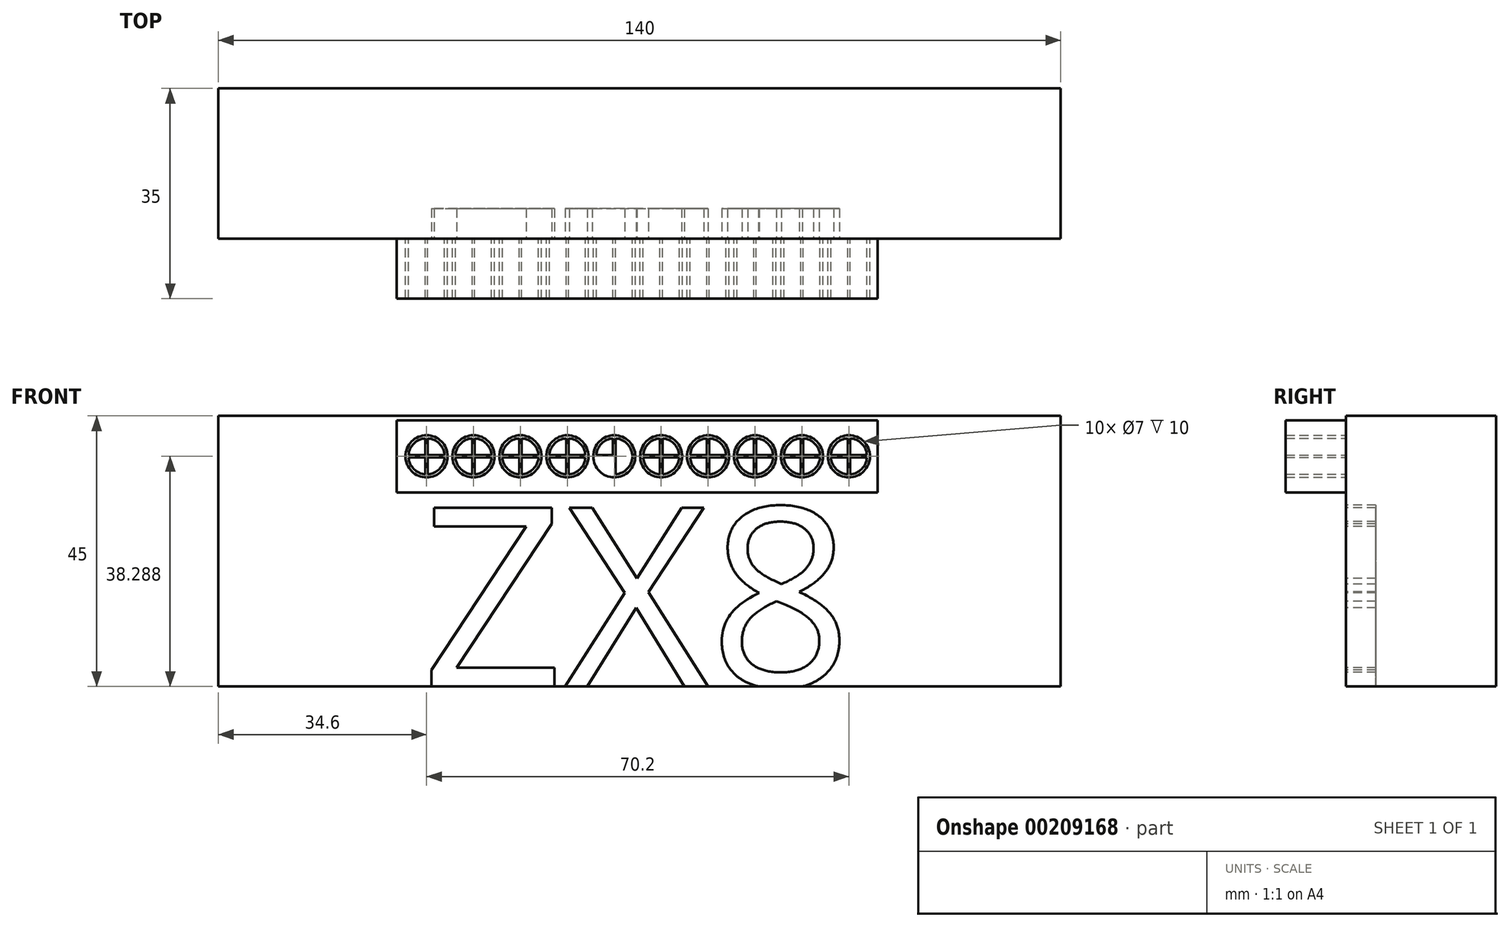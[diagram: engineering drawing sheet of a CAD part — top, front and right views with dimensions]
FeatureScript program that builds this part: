
annotation { "Feature Type Name" : "Feature", "Feature Type Description" : "" }
export const myFeature = defineFeature(function(context is Context, id is Id, definition is map)
    precondition{}
    {
        {
            var Q0;
            Q0=qCreatedBy(makeId("Front.planeOp"),FACE);
            var sketch = newSketch(context, id + "F0", { "sketchPlane" : qUnion([Q0])});
            skLineSegment(sketch, "E0.bottom", {"start": v(70, 22.5) * mm, "end": v(-70, 22.5) * mm});
            skLineSegment(sketch, "E0.top", {"start": v(70, -22.5) * mm, "end": v(-70, -22.5) * mm});
            skLineSegment(sketch, "E0.left", {"start": v(70, 22.5) * mm, "end": v(70, -22.5) * mm});
            skLineSegment(sketch, "E0.right", {"start": v(-70, 22.5) * mm, "end": v(-70, -22.5) * mm});
            skPoint(sketch, "E0.middle", {"position": v(0, 0) * mm});
            skSolve(sketch);
        }
        {
            var Q0;
            Q0 = qSketchRegion(id + "F0", true);
            extrude(context, id + "F1", {"entities" : qUnion([Q0]), "depth" : 25 * mm});
        }
        {
            var Q0;
            Q0=makeQuery(id+"F1.opExtrude","CAP_FACE",FACE,{"disambiguationData":[OSD([sQuery(id+"F0.wireOp",EDGE,"E0.bottom"),sQuery(id+"F0.wireOp",EDGE,"E0.top"),sQuery(id+"F0.wireOp",EDGE,"E0.left"),sQuery(id+"F0.wireOp",EDGE,"E0.right")])],"isStart":false});
            var sketch = newSketch(context, id + "F2", { "sketchPlane" : qUnion([Q0])});
            skText(sketch, "E1", { "text": "ZX8", "fontName": "OpenSans-Regular.ttf"});
            const initialGuessF2  = {"E1": [-0.03628, -0.0225, 1, 0, 0.03]};
            skSetInitialGuess(sketch, initialGuessF2);
            skSolve(sketch);
        }
        {
            var Q0;
            Q0 = qSketchRegion(id + "F2", true);
            extrude(context, id + "F3", {"entities" : qUnion([Q0]), "operationType" : NewBodyOperationType.REMOVE, "oppositeDirection" : true, "depth" : 5 * mm});
        }
        {
            var Q0;
            {var subQ0=sQuery(id+"F0.wireOp",EDGE,"E0.left");var subQ1=sQuery(id+"F0.wireOp",EDGE,"E0.bottom");var subQ2=sQuery(id+"F0.wireOp",EDGE,"E0.right");var subQ3=sQuery(id+"F0.wireOp",EDGE,"E0.top");Q0=makeQuery(id+"F3.boolean.opBoolean","SPLIT",FACE,{"disambiguationData":[TD([makeQuery(id+"F1.opExtrude","SWEPT_FACE",FACE,{"disambiguationData":[OSD([subQ1])]})])],"derivedFrom":makeQuery(id+"F1.opExtrude","CAP_FACE",FACE,{"disambiguationData":[OSD([subQ1,subQ3,subQ0,subQ2])],"isStart":false})});}
            var sketch = newSketch(context, id + "F4", { "sketchPlane" : qUnion([Q0])});
            skLineSegment(sketch, "E2.bottom", {"start": v(-40.4, 21.79) * mm, "end": v(39.6, 21.79) * mm});
            skLineSegment(sketch, "E2.top", {"start": v(-40.4, 9.79) * mm, "end": v(39.6, 9.79) * mm});
            skLineSegment(sketch, "E2.left", {"start": v(-40.4, 21.79) * mm, "end": v(-40.4, 9.79) * mm});
            skLineSegment(sketch, "E2.right", {"start": v(39.6, 21.79) * mm, "end": v(39.6, 9.79) * mm});
            skCircle(sketch, "E3", {"center": v(-35.4, 15.79) * mm, "radius": 3 * mm});
            skLineSegment(sketch, "E4.0", {"start": v(-35.6, 18.79) * mm, "end": v(-35.6, 12.79) * mm});
            skLineSegment(sketch, "E5.0", {"start": v(-35.2, 18.79) * mm, "end": v(-35.2, 12.79) * mm});
            skLineSegment(sketch, "E6.0", {"start": v(-38.4, 15.59) * mm, "end": v(-32.4, 15.59) * mm});
            skLineSegment(sketch, "E7.0", {"start": v(-38.4, 15.99) * mm, "end": v(-32.4, 15.99) * mm});
            skCircle(sketch, "E8.1.0.0", {"center": v(-27.6, 15.79) * mm, "radius": 3 * mm});
            skLineSegment(sketch, "E8.1.0.1", {"start": v(-30.6, 15.99) * mm, "end": v(-24.6, 15.99) * mm});
            skLineSegment(sketch, "E8.1.0.2", {"start": v(-27.4, 18.79) * mm, "end": v(-27.4, 12.79) * mm});
            skLineSegment(sketch, "E8.1.0.3", {"start": v(-27.8, 18.79) * mm, "end": v(-27.8, 12.79) * mm});
            skLineSegment(sketch, "E8.1.0.4", {"start": v(-30.6, 15.59) * mm, "end": v(-24.6, 15.59) * mm});
            skCircle(sketch, "E8.2.0.0", {"center": v(-19.8, 15.79) * mm, "radius": 3 * mm});
            skLineSegment(sketch, "E8.2.0.1", {"start": v(-22.8, 15.99) * mm, "end": v(-16.8, 15.99) * mm});
            skLineSegment(sketch, "E8.2.0.2", {"start": v(-19.6, 18.79) * mm, "end": v(-19.6, 12.79) * mm});
            skLineSegment(sketch, "E8.2.0.3", {"start": v(-20, 18.79) * mm, "end": v(-20, 12.79) * mm});
            skLineSegment(sketch, "E8.2.0.4", {"start": v(-22.8, 15.59) * mm, "end": v(-16.8, 15.59) * mm});
            skCircle(sketch, "E8.3.0.0", {"center": v(-12, 15.79) * mm, "radius": 3 * mm});
            skLineSegment(sketch, "E8.3.0.1", {"start": v(-15, 15.99) * mm, "end": v(-9, 15.99) * mm});
            skLineSegment(sketch, "E8.3.0.2", {"start": v(-11.8, 18.79) * mm, "end": v(-11.8, 12.79) * mm});
            skLineSegment(sketch, "E8.3.0.3", {"start": v(-12.2, 18.79) * mm, "end": v(-12.2, 12.79) * mm});
            skLineSegment(sketch, "E8.3.0.4", {"start": v(-15, 15.59) * mm, "end": v(-9, 15.59) * mm});
            skCircle(sketch, "E8.4.0.0", {"center": v(-4.2, 15.79) * mm, "radius": 3 * mm});
            skLineSegment(sketch, "E8.4.0.1", {"start": v(-7.2, 15.99) * mm, "end": v(-1.2, 15.99) * mm});
            skLineSegment(sketch, "E8.4.0.2", {"start": v(-4, 18.79) * mm, "end": v(-4, 12.79) * mm});
            skLineSegment(sketch, "E8.4.0.3", {"start": v(-4.4, 18.79) * mm, "end": v(-4.4, 12.79) * mm});
            skLineSegment(sketch, "E8.4.0.4", {"start": v(-7.2, 15.59) * mm, "end": v(-1.2, 15.59) * mm});
            skCircle(sketch, "E8.5.0.0", {"center": v(3.6, 15.79) * mm, "radius": 3 * mm});
            skLineSegment(sketch, "E8.5.0.1", {"start": v(0.6, 15.99) * mm, "end": v(6.6, 15.99) * mm});
            skLineSegment(sketch, "E8.5.0.2", {"start": v(3.8, 18.79) * mm, "end": v(3.8, 12.79) * mm});
            skLineSegment(sketch, "E8.5.0.3", {"start": v(3.4, 18.79) * mm, "end": v(3.4, 12.79) * mm});
            skLineSegment(sketch, "E8.5.0.4", {"start": v(0.6, 15.59) * mm, "end": v(6.6, 15.59) * mm});
            skCircle(sketch, "E8.6.0.0", {"center": v(11.4, 15.79) * mm, "radius": 3 * mm});
            skLineSegment(sketch, "E8.6.0.1", {"start": v(8.4, 15.99) * mm, "end": v(14.4, 15.99) * mm});
            skLineSegment(sketch, "E8.6.0.2", {"start": v(11.6, 18.79) * mm, "end": v(11.6, 12.79) * mm});
            skLineSegment(sketch, "E8.6.0.3", {"start": v(11.2, 18.79) * mm, "end": v(11.2, 12.79) * mm});
            skLineSegment(sketch, "E8.6.0.4", {"start": v(8.4, 15.59) * mm, "end": v(14.4, 15.59) * mm});
            skCircle(sketch, "E8.7.0.0", {"center": v(19.2, 15.79) * mm, "radius": 3 * mm});
            skLineSegment(sketch, "E8.7.0.1", {"start": v(16.2, 15.99) * mm, "end": v(22.2, 15.99) * mm});
            skLineSegment(sketch, "E8.7.0.2", {"start": v(19.4, 18.79) * mm, "end": v(19.4, 12.79) * mm});
            skLineSegment(sketch, "E8.7.0.3", {"start": v(19, 18.79) * mm, "end": v(19, 12.79) * mm});
            skLineSegment(sketch, "E8.7.0.4", {"start": v(16.2, 15.59) * mm, "end": v(22.2, 15.59) * mm});
            skCircle(sketch, "E8.8.0.0", {"center": v(27, 15.79) * mm, "radius": 3 * mm});
            skLineSegment(sketch, "E8.8.0.1", {"start": v(24, 15.99) * mm, "end": v(30, 15.99) * mm});
            skLineSegment(sketch, "E8.8.0.2", {"start": v(27.2, 18.79) * mm, "end": v(27.2, 12.79) * mm});
            skLineSegment(sketch, "E8.8.0.3", {"start": v(26.8, 18.79) * mm, "end": v(26.8, 12.79) * mm});
            skLineSegment(sketch, "E8.8.0.4", {"start": v(24, 15.59) * mm, "end": v(30, 15.59) * mm});
            skCircle(sketch, "E8.9.0.0", {"center": v(34.8, 15.79) * mm, "radius": 3 * mm});
            skLineSegment(sketch, "E8.9.0.1", {"start": v(31.8, 15.99) * mm, "end": v(37.8, 15.99) * mm});
            skLineSegment(sketch, "E8.9.0.2", {"start": v(35, 18.79) * mm, "end": v(35, 12.79) * mm});
            skLineSegment(sketch, "E8.9.0.3", {"start": v(34.6, 18.79) * mm, "end": v(34.6, 12.79) * mm});
            skLineSegment(sketch, "E8.9.0.4", {"start": v(31.8, 15.59) * mm, "end": v(37.8, 15.59) * mm});
            skLineSegment(sketch, "E8.direction1", {"start": v(-35.4, 15.79) * mm, "end": v(-27.6, 15.79) * mm, "construction": true});
            skCircle(sketch, "E9", {"center": v(-35.4, 15.79) * mm, "radius": 3.5 * mm});
            skCircle(sketch, "E10.1.0.0", {"center": v(-27.6, 15.79) * mm, "radius": 3.5 * mm});
            skCircle(sketch, "E10.2.0.0", {"center": v(-19.8, 15.79) * mm, "radius": 3.5 * mm});
            skCircle(sketch, "E10.3.0.0", {"center": v(-12, 15.79) * mm, "radius": 3.5 * mm});
            skCircle(sketch, "E10.4.0.0", {"center": v(-4.2, 15.79) * mm, "radius": 3.5 * mm});
            skCircle(sketch, "E10.5.0.0", {"center": v(3.6, 15.79) * mm, "radius": 3.5 * mm});
            skCircle(sketch, "E10.6.0.0", {"center": v(11.4, 15.79) * mm, "radius": 3.5 * mm});
            skCircle(sketch, "E10.7.0.0", {"center": v(19.2, 15.79) * mm, "radius": 3.5 * mm});
            skCircle(sketch, "E10.8.0.0", {"center": v(27, 15.79) * mm, "radius": 3.5 * mm});
            skCircle(sketch, "E10.9.0.0", {"center": v(34.8, 15.79) * mm, "radius": 3.5 * mm});
            skSolve(sketch);
        }
        {
            var Q0;
            Q0 = qSketchRegion(id + "F4", true);
            var Q1;
            {var subQ0=sQuery(id+"F4.wireOp",EDGE,"E4.0");var subQ1=sQuery(id+"F4.wireOp",EDGE,"E3");var subQ2=makeQuery(id+"F4.imprint","INTERSECT",VERTEX,{"disambiguationData":[OD(0.0)],"derivedFrom":[subQ1,subQ0]});Q1=makeQuery(id+"F4.imprint","IMPRINT",FACE,{"disambiguationData":[TD([[makeQuery(id+"F4.imprint","IMPRINT",EDGE,{"disambiguationData":[TD([[subQ2,-1.0]])],"derivedFrom":subQ1}),1.0]])]});}
            var Q2;
            {var subQ0=sQuery(id+"F4.wireOp",EDGE,"E5.0");var subQ1=sQuery(id+"F4.wireOp",EDGE,"E3");var subQ2=makeQuery(id+"F4.imprint","INTERSECT",VERTEX,{"disambiguationData":[OD(0.0)],"derivedFrom":[subQ1,subQ0]});Q2=makeQuery(id+"F4.imprint","IMPRINT",FACE,{"disambiguationData":[TD([[makeQuery(id+"F4.imprint","IMPRINT",EDGE,{"disambiguationData":[TD([[subQ2,1.0]])],"derivedFrom":subQ1}),1.0]])]});}
            var Q3;
            {var subQ0=sQuery(id+"F4.wireOp",EDGE,"E5.0");var subQ1=sQuery(id+"F4.wireOp",EDGE,"E3");var subQ2=makeQuery(id+"F4.imprint","INTERSECT",VERTEX,{"disambiguationData":[OD(1.0)],"derivedFrom":[subQ1,subQ0]});Q3=makeQuery(id+"F4.imprint","IMPRINT",FACE,{"disambiguationData":[TD([[makeQuery(id+"F4.imprint","IMPRINT",EDGE,{"disambiguationData":[TD([[subQ2,-1.0]])],"derivedFrom":subQ1}),1.0]])]});}
            var Q4;
            {var subQ0=sQuery(id+"F4.wireOp",EDGE,"E6.0");var subQ1=sQuery(id+"F4.wireOp",EDGE,"E3");var subQ2=makeQuery(id+"F4.imprint","INTERSECT",VERTEX,{"disambiguationData":[OD(0.0)],"derivedFrom":[subQ1,subQ0]});Q4=makeQuery(id+"F4.imprint","IMPRINT",FACE,{"disambiguationData":[TD([[makeQuery(id+"F4.imprint","IMPRINT",EDGE,{"disambiguationData":[TD([[subQ2,-1.0]])],"derivedFrom":subQ1}),1.0]])]});}
            var Q5;
            {var subQ0=sQuery(id+"F4.wireOp",EDGE,"E8.1.0.3");var subQ1=sQuery(id+"F4.wireOp",EDGE,"E8.1.0.0");var subQ2=makeQuery(id+"F4.imprint","INTERSECT",VERTEX,{"disambiguationData":[OD(0.0)],"derivedFrom":[subQ1,subQ0]});Q5=makeQuery(id+"F4.imprint","IMPRINT",FACE,{"disambiguationData":[TD([[makeQuery(id+"F4.imprint","IMPRINT",EDGE,{"disambiguationData":[TD([[subQ2,-1.0]])],"derivedFrom":subQ1}),1.0]])]});}
            var Q6;
            {var subQ0=sQuery(id+"F4.wireOp",EDGE,"E8.1.0.2");var subQ1=sQuery(id+"F4.wireOp",EDGE,"E8.1.0.0");var subQ2=makeQuery(id+"F4.imprint","INTERSECT",VERTEX,{"disambiguationData":[OD(0.0)],"derivedFrom":[subQ1,subQ0]});Q6=makeQuery(id+"F4.imprint","IMPRINT",FACE,{"disambiguationData":[TD([[makeQuery(id+"F4.imprint","IMPRINT",EDGE,{"disambiguationData":[TD([[subQ2,1.0]])],"derivedFrom":subQ1}),1.0]])]});}
            var Q7;
            {var subQ0=sQuery(id+"F4.wireOp",EDGE,"E8.1.0.2");var subQ1=sQuery(id+"F4.wireOp",EDGE,"E8.1.0.0");var subQ2=makeQuery(id+"F4.imprint","INTERSECT",VERTEX,{"disambiguationData":[OD(1.0)],"derivedFrom":[subQ1,subQ0]});Q7=makeQuery(id+"F4.imprint","IMPRINT",FACE,{"disambiguationData":[TD([[makeQuery(id+"F4.imprint","IMPRINT",EDGE,{"disambiguationData":[TD([[subQ2,-1.0]])],"derivedFrom":subQ1}),1.0]])]});}
            var Q8;
            {var subQ0=sQuery(id+"F4.wireOp",EDGE,"E8.1.0.4");var subQ1=sQuery(id+"F4.wireOp",EDGE,"E8.1.0.0");var subQ2=makeQuery(id+"F4.imprint","INTERSECT",VERTEX,{"disambiguationData":[OD(0.0)],"derivedFrom":[subQ1,subQ0]});Q8=makeQuery(id+"F4.imprint","IMPRINT",FACE,{"disambiguationData":[TD([[makeQuery(id+"F4.imprint","IMPRINT",EDGE,{"disambiguationData":[TD([[subQ2,-1.0]])],"derivedFrom":subQ1}),1.0]])]});}
            var Q9;
            {var subQ0=sQuery(id+"F4.wireOp",EDGE,"E8.2.0.4");var subQ1=sQuery(id+"F4.wireOp",EDGE,"E8.2.0.0");var subQ2=makeQuery(id+"F4.imprint","INTERSECT",VERTEX,{"disambiguationData":[OD(0.0)],"derivedFrom":[subQ1,subQ0]});Q9=makeQuery(id+"F4.imprint","IMPRINT",FACE,{"disambiguationData":[TD([[makeQuery(id+"F4.imprint","IMPRINT",EDGE,{"disambiguationData":[TD([[subQ2,-1.0]])],"derivedFrom":subQ1}),1.0]])]});}
            var Q10;
            {var subQ0=sQuery(id+"F4.wireOp",EDGE,"E8.2.0.3");var subQ1=sQuery(id+"F4.wireOp",EDGE,"E8.2.0.0");var subQ2=makeQuery(id+"F4.imprint","INTERSECT",VERTEX,{"disambiguationData":[OD(0.0)],"derivedFrom":[subQ1,subQ0]});Q10=makeQuery(id+"F4.imprint","IMPRINT",FACE,{"disambiguationData":[TD([[makeQuery(id+"F4.imprint","IMPRINT",EDGE,{"disambiguationData":[TD([[subQ2,-1.0]])],"derivedFrom":subQ1}),1.0]])]});}
            var Q11;
            {var subQ0=sQuery(id+"F4.wireOp",EDGE,"E8.2.0.2");var subQ1=sQuery(id+"F4.wireOp",EDGE,"E8.2.0.0");var subQ2=makeQuery(id+"F4.imprint","INTERSECT",VERTEX,{"disambiguationData":[OD(0.0)],"derivedFrom":[subQ1,subQ0]});Q11=makeQuery(id+"F4.imprint","IMPRINT",FACE,{"disambiguationData":[TD([[makeQuery(id+"F4.imprint","IMPRINT",EDGE,{"disambiguationData":[TD([[subQ2,1.0]])],"derivedFrom":subQ1}),1.0]])]});}
            var Q12;
            {var subQ0=sQuery(id+"F4.wireOp",EDGE,"E8.2.0.2");var subQ1=sQuery(id+"F4.wireOp",EDGE,"E8.2.0.0");var subQ2=makeQuery(id+"F4.imprint","INTERSECT",VERTEX,{"disambiguationData":[OD(1.0)],"derivedFrom":[subQ1,subQ0]});Q12=makeQuery(id+"F4.imprint","IMPRINT",FACE,{"disambiguationData":[TD([[makeQuery(id+"F4.imprint","IMPRINT",EDGE,{"disambiguationData":[TD([[subQ2,-1.0]])],"derivedFrom":subQ1}),1.0]])]});}
            var Q13;
            {var subQ0=sQuery(id+"F4.wireOp",EDGE,"E8.3.0.4");var subQ1=sQuery(id+"F4.wireOp",EDGE,"E8.3.0.0");var subQ2=makeQuery(id+"F4.imprint","INTERSECT",VERTEX,{"disambiguationData":[OD(0.0)],"derivedFrom":[subQ1,subQ0]});Q13=makeQuery(id+"F4.imprint","IMPRINT",FACE,{"disambiguationData":[TD([[makeQuery(id+"F4.imprint","IMPRINT",EDGE,{"disambiguationData":[TD([[subQ2,-1.0]])],"derivedFrom":subQ1}),1.0]])]});}
            var Q14;
            {var subQ0=sQuery(id+"F4.wireOp",EDGE,"E8.3.0.3");var subQ1=sQuery(id+"F4.wireOp",EDGE,"E8.3.0.0");var subQ2=makeQuery(id+"F4.imprint","INTERSECT",VERTEX,{"disambiguationData":[OD(0.0)],"derivedFrom":[subQ1,subQ0]});Q14=makeQuery(id+"F4.imprint","IMPRINT",FACE,{"disambiguationData":[TD([[makeQuery(id+"F4.imprint","IMPRINT",EDGE,{"disambiguationData":[TD([[subQ2,-1.0]])],"derivedFrom":subQ1}),1.0]])]});}
            var Q15;
            {var subQ0=sQuery(id+"F4.wireOp",EDGE,"E8.3.0.2");var subQ1=sQuery(id+"F4.wireOp",EDGE,"E8.3.0.0");var subQ2=makeQuery(id+"F4.imprint","INTERSECT",VERTEX,{"disambiguationData":[OD(0.0)],"derivedFrom":[subQ1,subQ0]});Q15=makeQuery(id+"F4.imprint","IMPRINT",FACE,{"disambiguationData":[TD([[makeQuery(id+"F4.imprint","IMPRINT",EDGE,{"disambiguationData":[TD([[subQ2,1.0]])],"derivedFrom":subQ1}),1.0]])]});}
            var Q16;
            {var subQ0=sQuery(id+"F4.wireOp",EDGE,"E8.3.0.2");var subQ1=sQuery(id+"F4.wireOp",EDGE,"E8.3.0.0");var subQ2=makeQuery(id+"F4.imprint","INTERSECT",VERTEX,{"disambiguationData":[OD(1.0)],"derivedFrom":[subQ1,subQ0]});Q16=makeQuery(id+"F4.imprint","IMPRINT",FACE,{"disambiguationData":[TD([[makeQuery(id+"F4.imprint","IMPRINT",EDGE,{"disambiguationData":[TD([[subQ2,-1.0]])],"derivedFrom":subQ1}),1.0]])]});}
            var Q17;
            {var subQ0=sQuery(id+"F4.wireOp",EDGE,"E8.4.0.4");var subQ1=sQuery(id+"F4.wireOp",EDGE,"E8.4.0.0");var subQ2=makeQuery(id+"F4.imprint","INTERSECT",VERTEX,{"disambiguationData":[OD(0.0)],"derivedFrom":[subQ1,subQ0]});Q17=makeQuery(id+"F4.imprint","IMPRINT",FACE,{"disambiguationData":[TD([[makeQuery(id+"F4.imprint","IMPRINT",EDGE,{"disambiguationData":[TD([[subQ2,-1.0]])],"derivedFrom":subQ1}),1.0]])]});}
            var Q18;
            {var subQ0=sQuery(id+"F4.wireOp",EDGE,"E8.4.0.3");var subQ1=sQuery(id+"F4.wireOp",EDGE,"E8.4.0.0");var subQ2=makeQuery(id+"F4.imprint","INTERSECT",VERTEX,{"disambiguationData":[OD(0.0)],"derivedFrom":[subQ1,subQ0]});Q18=makeQuery(id+"F4.imprint","IMPRINT",FACE,{"disambiguationData":[TD([[makeQuery(id+"F4.imprint","IMPRINT",EDGE,{"disambiguationData":[TD([[subQ2,-1.0]])],"derivedFrom":subQ1}),1.0]])]});}
            var Q19;
            {var subQ0=sQuery(id+"F4.wireOp",EDGE,"E8.4.0.2");var subQ1=sQuery(id+"F4.wireOp",EDGE,"E8.4.0.0");var subQ2=makeQuery(id+"F4.imprint","INTERSECT",VERTEX,{"disambiguationData":[OD(0.0)],"derivedFrom":[subQ1,subQ0]});Q19=makeQuery(id+"F4.imprint","IMPRINT",FACE,{"disambiguationData":[TD([[makeQuery(id+"F4.imprint","IMPRINT",EDGE,{"disambiguationData":[TD([[subQ2,1.0]])],"derivedFrom":subQ1}),1.0]])]});}
            var Q20;
            {var subQ0=sQuery(id+"F4.wireOp",EDGE,"E8.4.0.2");var subQ1=sQuery(id+"F4.wireOp",EDGE,"E8.4.0.0");var subQ2=makeQuery(id+"F4.imprint","INTERSECT",VERTEX,{"disambiguationData":[OD(1.0)],"derivedFrom":[subQ1,subQ0]});Q20=makeQuery(id+"F4.imprint","IMPRINT",FACE,{"disambiguationData":[TD([[makeQuery(id+"F4.imprint","IMPRINT",EDGE,{"disambiguationData":[TD([[subQ2,-1.0]])],"derivedFrom":subQ1}),1.0]])]});}
            var Q21;
            {var subQ0=sQuery(id+"F4.wireOp",EDGE,"E8.5.0.4");var subQ1=sQuery(id+"F4.wireOp",EDGE,"E8.5.0.0");var subQ2=makeQuery(id+"F4.imprint","INTERSECT",VERTEX,{"disambiguationData":[OD(0.0)],"derivedFrom":[subQ1,subQ0]});Q21=makeQuery(id+"F4.imprint","IMPRINT",FACE,{"disambiguationData":[TD([[makeQuery(id+"F4.imprint","IMPRINT",EDGE,{"disambiguationData":[TD([[subQ2,-1.0]])],"derivedFrom":subQ1}),1.0]])]});}
            var Q22;
            {var subQ0=sQuery(id+"F4.wireOp",EDGE,"E8.5.0.3");var subQ1=sQuery(id+"F4.wireOp",EDGE,"E8.5.0.0");var subQ2=makeQuery(id+"F4.imprint","INTERSECT",VERTEX,{"disambiguationData":[OD(0.0)],"derivedFrom":[subQ1,subQ0]});Q22=makeQuery(id+"F4.imprint","IMPRINT",FACE,{"disambiguationData":[TD([[makeQuery(id+"F4.imprint","IMPRINT",EDGE,{"disambiguationData":[TD([[subQ2,-1.0]])],"derivedFrom":subQ1}),1.0]])]});}
            var Q23;
            {var subQ0=sQuery(id+"F4.wireOp",EDGE,"E8.5.0.2");var subQ1=sQuery(id+"F4.wireOp",EDGE,"E8.5.0.0");var subQ2=makeQuery(id+"F4.imprint","INTERSECT",VERTEX,{"disambiguationData":[OD(0.0)],"derivedFrom":[subQ1,subQ0]});Q23=makeQuery(id+"F4.imprint","IMPRINT",FACE,{"disambiguationData":[TD([[makeQuery(id+"F4.imprint","IMPRINT",EDGE,{"disambiguationData":[TD([[subQ2,1.0]])],"derivedFrom":subQ1}),1.0]])]});}
            var Q24;
            {var subQ0=sQuery(id+"F4.wireOp",EDGE,"E8.5.0.2");var subQ1=sQuery(id+"F4.wireOp",EDGE,"E8.5.0.0");var subQ2=makeQuery(id+"F4.imprint","INTERSECT",VERTEX,{"disambiguationData":[OD(1.0)],"derivedFrom":[subQ1,subQ0]});Q24=makeQuery(id+"F4.imprint","IMPRINT",FACE,{"disambiguationData":[TD([[makeQuery(id+"F4.imprint","IMPRINT",EDGE,{"disambiguationData":[TD([[subQ2,-1.0]])],"derivedFrom":subQ1}),1.0]])]});}
            var Q25;
            {var subQ0=sQuery(id+"F4.wireOp",EDGE,"E8.6.0.3");var subQ1=sQuery(id+"F4.wireOp",EDGE,"E8.6.0.0");var subQ2=makeQuery(id+"F4.imprint","INTERSECT",VERTEX,{"disambiguationData":[OD(0.0)],"derivedFrom":[subQ1,subQ0]});Q25=makeQuery(id+"F4.imprint","IMPRINT",FACE,{"disambiguationData":[TD([[makeQuery(id+"F4.imprint","IMPRINT",EDGE,{"disambiguationData":[TD([[subQ2,-1.0]])],"derivedFrom":subQ1}),1.0]])]});}
            var Q26;
            {var subQ0=sQuery(id+"F4.wireOp",EDGE,"E8.6.0.2");var subQ1=sQuery(id+"F4.wireOp",EDGE,"E8.6.0.0");var subQ2=makeQuery(id+"F4.imprint","INTERSECT",VERTEX,{"disambiguationData":[OD(0.0)],"derivedFrom":[subQ1,subQ0]});Q26=makeQuery(id+"F4.imprint","IMPRINT",FACE,{"disambiguationData":[TD([[makeQuery(id+"F4.imprint","IMPRINT",EDGE,{"disambiguationData":[TD([[subQ2,1.0]])],"derivedFrom":subQ1}),1.0]])]});}
            var Q27;
            {var subQ0=sQuery(id+"F4.wireOp",EDGE,"E8.6.0.2");var subQ1=sQuery(id+"F4.wireOp",EDGE,"E8.6.0.0");var subQ2=makeQuery(id+"F4.imprint","INTERSECT",VERTEX,{"disambiguationData":[OD(1.0)],"derivedFrom":[subQ1,subQ0]});Q27=makeQuery(id+"F4.imprint","IMPRINT",FACE,{"disambiguationData":[TD([[makeQuery(id+"F4.imprint","IMPRINT",EDGE,{"disambiguationData":[TD([[subQ2,-1.0]])],"derivedFrom":subQ1}),1.0]])]});}
            var Q28;
            {var subQ0=sQuery(id+"F4.wireOp",EDGE,"E8.6.0.4");var subQ1=sQuery(id+"F4.wireOp",EDGE,"E8.6.0.0");var subQ2=makeQuery(id+"F4.imprint","INTERSECT",VERTEX,{"disambiguationData":[OD(0.0)],"derivedFrom":[subQ1,subQ0]});Q28=makeQuery(id+"F4.imprint","IMPRINT",FACE,{"disambiguationData":[TD([[makeQuery(id+"F4.imprint","IMPRINT",EDGE,{"disambiguationData":[TD([[subQ2,-1.0]])],"derivedFrom":subQ1}),1.0]])]});}
            var Q29;
            {var subQ0=sQuery(id+"F4.wireOp",EDGE,"E8.7.0.3");var subQ1=sQuery(id+"F4.wireOp",EDGE,"E8.7.0.0");var subQ2=makeQuery(id+"F4.imprint","INTERSECT",VERTEX,{"disambiguationData":[OD(0.0)],"derivedFrom":[subQ1,subQ0]});Q29=makeQuery(id+"F4.imprint","IMPRINT",FACE,{"disambiguationData":[TD([[makeQuery(id+"F4.imprint","IMPRINT",EDGE,{"disambiguationData":[TD([[subQ2,-1.0]])],"derivedFrom":subQ1}),1.0]])]});}
            var Q30;
            {var subQ0=sQuery(id+"F4.wireOp",EDGE,"E8.7.0.2");var subQ1=sQuery(id+"F4.wireOp",EDGE,"E8.7.0.0");var subQ2=makeQuery(id+"F4.imprint","INTERSECT",VERTEX,{"disambiguationData":[OD(0.0)],"derivedFrom":[subQ1,subQ0]});Q30=makeQuery(id+"F4.imprint","IMPRINT",FACE,{"disambiguationData":[TD([[makeQuery(id+"F4.imprint","IMPRINT",EDGE,{"disambiguationData":[TD([[subQ2,1.0]])],"derivedFrom":subQ1}),1.0]])]});}
            var Q31;
            {var subQ0=sQuery(id+"F4.wireOp",EDGE,"E8.7.0.2");var subQ1=sQuery(id+"F4.wireOp",EDGE,"E8.7.0.0");var subQ2=makeQuery(id+"F4.imprint","INTERSECT",VERTEX,{"disambiguationData":[OD(1.0)],"derivedFrom":[subQ1,subQ0]});Q31=makeQuery(id+"F4.imprint","IMPRINT",FACE,{"disambiguationData":[TD([[makeQuery(id+"F4.imprint","IMPRINT",EDGE,{"disambiguationData":[TD([[subQ2,-1.0]])],"derivedFrom":subQ1}),1.0]])]});}
            var Q32;
            {var subQ0=sQuery(id+"F4.wireOp",EDGE,"E8.7.0.4");var subQ1=sQuery(id+"F4.wireOp",EDGE,"E8.7.0.0");var subQ2=makeQuery(id+"F4.imprint","INTERSECT",VERTEX,{"disambiguationData":[OD(0.0)],"derivedFrom":[subQ1,subQ0]});Q32=makeQuery(id+"F4.imprint","IMPRINT",FACE,{"disambiguationData":[TD([[makeQuery(id+"F4.imprint","IMPRINT",EDGE,{"disambiguationData":[TD([[subQ2,-1.0]])],"derivedFrom":subQ1}),1.0]])]});}
            var Q33;
            {var subQ0=sQuery(id+"F4.wireOp",EDGE,"E8.8.0.3");var subQ1=sQuery(id+"F4.wireOp",EDGE,"E8.8.0.0");var subQ2=makeQuery(id+"F4.imprint","INTERSECT",VERTEX,{"disambiguationData":[OD(0.0)],"derivedFrom":[subQ1,subQ0]});Q33=makeQuery(id+"F4.imprint","IMPRINT",FACE,{"disambiguationData":[TD([[makeQuery(id+"F4.imprint","IMPRINT",EDGE,{"disambiguationData":[TD([[subQ2,-1.0]])],"derivedFrom":subQ1}),1.0]])]});}
            var Q34;
            {var subQ0=sQuery(id+"F4.wireOp",EDGE,"E8.8.0.2");var subQ1=sQuery(id+"F4.wireOp",EDGE,"E8.8.0.0");var subQ2=makeQuery(id+"F4.imprint","INTERSECT",VERTEX,{"disambiguationData":[OD(0.0)],"derivedFrom":[subQ1,subQ0]});Q34=makeQuery(id+"F4.imprint","IMPRINT",FACE,{"disambiguationData":[TD([[makeQuery(id+"F4.imprint","IMPRINT",EDGE,{"disambiguationData":[TD([[subQ2,1.0]])],"derivedFrom":subQ1}),1.0]])]});}
            var Q35;
            {var subQ0=sQuery(id+"F4.wireOp",EDGE,"E8.8.0.2");var subQ1=sQuery(id+"F4.wireOp",EDGE,"E8.8.0.0");var subQ2=makeQuery(id+"F4.imprint","INTERSECT",VERTEX,{"disambiguationData":[OD(1.0)],"derivedFrom":[subQ1,subQ0]});Q35=makeQuery(id+"F4.imprint","IMPRINT",FACE,{"disambiguationData":[TD([[makeQuery(id+"F4.imprint","IMPRINT",EDGE,{"disambiguationData":[TD([[subQ2,-1.0]])],"derivedFrom":subQ1}),1.0]])]});}
            var Q36;
            {var subQ0=sQuery(id+"F4.wireOp",EDGE,"E8.8.0.4");var subQ1=sQuery(id+"F4.wireOp",EDGE,"E8.8.0.0");var subQ2=makeQuery(id+"F4.imprint","INTERSECT",VERTEX,{"disambiguationData":[OD(0.0)],"derivedFrom":[subQ1,subQ0]});Q36=makeQuery(id+"F4.imprint","IMPRINT",FACE,{"disambiguationData":[TD([[makeQuery(id+"F4.imprint","IMPRINT",EDGE,{"disambiguationData":[TD([[subQ2,-1.0]])],"derivedFrom":subQ1}),1.0]])]});}
            var Q37;
            {var subQ0=sQuery(id+"F4.wireOp",EDGE,"E8.9.0.3");var subQ1=sQuery(id+"F4.wireOp",EDGE,"E8.9.0.0");var subQ2=makeQuery(id+"F4.imprint","INTERSECT",VERTEX,{"disambiguationData":[OD(0.0)],"derivedFrom":[subQ1,subQ0]});Q37=makeQuery(id+"F4.imprint","IMPRINT",FACE,{"disambiguationData":[TD([[makeQuery(id+"F4.imprint","IMPRINT",EDGE,{"disambiguationData":[TD([[subQ2,-1.0]])],"derivedFrom":subQ1}),1.0]])]});}
            var Q38;
            {var subQ0=sQuery(id+"F4.wireOp",EDGE,"E8.9.0.2");var subQ1=sQuery(id+"F4.wireOp",EDGE,"E8.9.0.0");var subQ2=makeQuery(id+"F4.imprint","INTERSECT",VERTEX,{"disambiguationData":[OD(0.0)],"derivedFrom":[subQ1,subQ0]});Q38=makeQuery(id+"F4.imprint","IMPRINT",FACE,{"disambiguationData":[TD([[makeQuery(id+"F4.imprint","IMPRINT",EDGE,{"disambiguationData":[TD([[subQ2,1.0]])],"derivedFrom":subQ1}),1.0]])]});}
            var Q39;
            {var subQ0=sQuery(id+"F4.wireOp",EDGE,"E8.9.0.2");var subQ1=sQuery(id+"F4.wireOp",EDGE,"E8.9.0.0");var subQ2=makeQuery(id+"F4.imprint","INTERSECT",VERTEX,{"disambiguationData":[OD(1.0)],"derivedFrom":[subQ1,subQ0]});Q39=makeQuery(id+"F4.imprint","IMPRINT",FACE,{"disambiguationData":[TD([[makeQuery(id+"F4.imprint","IMPRINT",EDGE,{"disambiguationData":[TD([[subQ2,-1.0]])],"derivedFrom":subQ1}),1.0]])]});}
            var Q40;
            {var subQ0=sQuery(id+"F4.wireOp",EDGE,"E8.9.0.4");var subQ1=sQuery(id+"F4.wireOp",EDGE,"E8.9.0.0");var subQ2=makeQuery(id+"F4.imprint","INTERSECT",VERTEX,{"disambiguationData":[OD(0.0)],"derivedFrom":[subQ1,subQ0]});Q40=makeQuery(id+"F4.imprint","IMPRINT",FACE,{"disambiguationData":[TD([[makeQuery(id+"F4.imprint","IMPRINT",EDGE,{"disambiguationData":[TD([[subQ2,-1.0]])],"derivedFrom":subQ1}),1.0]])]});}
            extrude(context, id + "F5", {"entities" : qUnion([Q0, Q1, Q2, Q3, Q4, Q5, Q6, Q7, Q8, Q9, Q10, Q11, Q12, Q13, Q14, Q15, Q16, Q17, Q18, Q19, Q20, Q21, Q22, Q23, Q24, Q25, Q26, Q27, Q28, Q29, Q30, Q31, Q32, Q33, Q34, Q35, Q36, Q37, Q38, Q39, Q40]), "operationType" : NewBodyOperationType.ADD, "depth" : 10 * mm});
        }
    });
